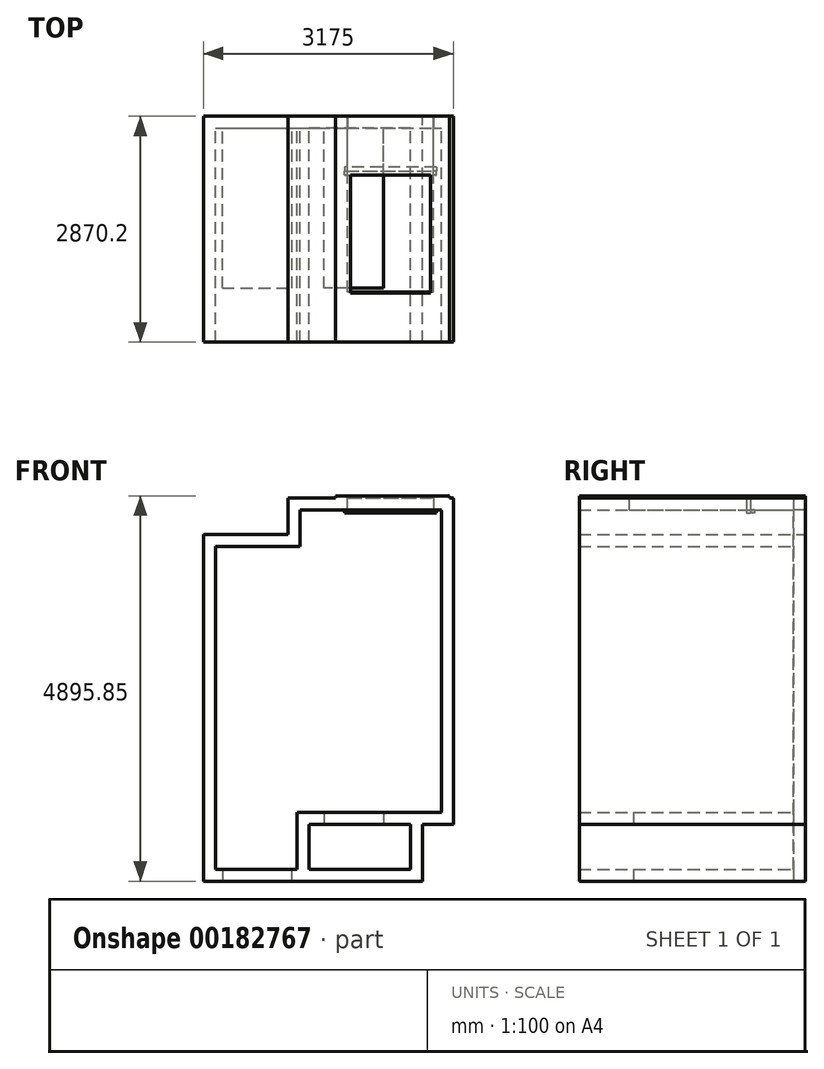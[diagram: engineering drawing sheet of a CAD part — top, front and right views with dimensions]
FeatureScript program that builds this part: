
annotation { "Feature Type Name" : "Feature", "Feature Type Description" : "" }
export const myFeature = defineFeature(function(context is Context, id is Id, definition is map)
    precondition{}
    {
        {
            var Q0;
            Q0=qCreatedBy(makeId("Front.planeOp"),FACE);
            var sketch = newSketch(context, id + "F0", { "sketchPlane" : qUnion([Q0])});
            skLineSegment(sketch, "E0", {"start": v(0, 0) * mm, "end": v(0, 4102.1) * mm});
            skLineSegment(sketch, "E1", {"start": v(0, 0) * mm, "end": v(88.9, 0) * mm});
            skLineSegment(sketch, "E2", {"start": v(88.9, 0) * mm, "end": v(88.9, -152.4) * mm});
            skLineSegment(sketch, "E3", {"start": v(88.9, -152.4) * mm, "end": v(-152.4, -152.4) * mm});
            skLineSegment(sketch, "E4", {"start": v(-152.4, -152.4) * mm, "end": v(-152.4, 4254.5) * mm});
            skLineSegment(sketch, "E5", {"start": v(0, 4102.1) * mm, "end": v(1073.15, 4102.1) * mm});
            skLineSegment(sketch, "E6", {"start": v(-152.4, 4254.5) * mm, "end": v(920.75, 4254.5) * mm});
            skLineSegment(sketch, "E7", {"start": v(1073.15, 4102.1) * mm, "end": v(1073.15, 4565.65) * mm});
            skLineSegment(sketch, "E8", {"start": v(920.75, 4254.5) * mm, "end": v(920.75, 4718.05) * mm});
            skLineSegment(sketch, "E9", {"start": v(1073.15, 4565.65) * mm, "end": v(1676.4, 4565.65) * mm});
            skLineSegment(sketch, "E10", {"start": v(920.75, 4718.05) * mm, "end": v(1524, 4718.05) * mm});
            skLineSegment(sketch, "E11", {"start": v(1524, 4718.05) * mm, "end": v(1524, 4743.45) * mm});
            skLineSegment(sketch, "E12", {"start": v(1524, 4743.45) * mm, "end": v(2971.8, 4743.45) * mm});
            skLineSegment(sketch, "E13", {"start": v(1676.4, 4565.65) * mm, "end": v(1676.4, 4718.05) * mm});
            skLineSegment(sketch, "E14", {"start": v(1676.4, 4718.05) * mm, "end": v(2768.6, 4718.05) * mm});
            skLineSegment(sketch, "E15", {"start": v(2971.8, 4743.45) * mm, "end": v(2971.8, 4718.05) * mm});
            skLineSegment(sketch, "E16", {"start": v(2768.6, 4718.05) * mm, "end": v(2768.6, 4565.65) * mm});
            skLineSegment(sketch, "E17", {"start": v(2768.6, 4565.65) * mm, "end": v(2870.2, 4565.65) * mm});
            skLineSegment(sketch, "E18", {"start": v(2971.8, 4718.05) * mm, "end": v(3022.6, 4718.05) * mm});
            skLineSegment(sketch, "E19", {"start": v(2870.2, 4565.65) * mm, "end": v(2870.2, 723.9) * mm});
            skLineSegment(sketch, "E20", {"start": v(2870.2, 723.9) * mm, "end": v(2133.6, 723.9) * mm});
            skLineSegment(sketch, "E21", {"start": v(2133.6, 723.9) * mm, "end": v(2133.6, 571.5) * mm});
            skLineSegment(sketch, "E22", {"start": v(2133.6, 571.5) * mm, "end": v(2476.5, 571.5) * mm});
            skLineSegment(sketch, "E23", {"start": v(88.9, 0) * mm, "end": v(971.55, 0) * mm});
            skLineSegment(sketch, "E24", {"start": v(88.9, -152.4) * mm, "end": v(971.55, -152.4) * mm});
            skLineSegment(sketch, "E25", {"start": v(971.55, -152.4) * mm, "end": v(971.55, 0) * mm});
            skLineSegment(sketch, "E26", {"start": v(971.55, 0) * mm, "end": v(1035.05, 0) * mm});
            skLineSegment(sketch, "E27", {"start": v(2476.5, 571.5) * mm, "end": v(2476.5, 0) * mm});
            skLineSegment(sketch, "E28", {"start": v(2476.5, 0) * mm, "end": v(1187.45, 0) * mm});
            skLineSegment(sketch, "E29", {"start": v(1035.05, 0) * mm, "end": v(1035.05, 723.9) * mm});
            skLineSegment(sketch, "E30", {"start": v(1035.05, 723.9) * mm, "end": v(1339.85, 723.9) * mm});
            skLineSegment(sketch, "E31", {"start": v(1187.45, 0) * mm, "end": v(1187.45, 571.5) * mm});
            skLineSegment(sketch, "E32", {"start": v(2133.6, 723.9) * mm, "end": v(1377.95, 723.9) * mm});
            skLineSegment(sketch, "E33", {"start": v(2133.6, 571.5) * mm, "end": v(1377.95, 571.5) * mm});
            skLineSegment(sketch, "E34", {"start": v(1377.95, 723.9) * mm, "end": v(1377.95, 571.5) * mm});
            skLineSegment(sketch, "E35", {"start": v(1187.45, 571.5) * mm, "end": v(1339.85, 571.5) * mm});
            skLineSegment(sketch, "E36", {"start": v(1339.85, 723.9) * mm, "end": v(1339.85, 571.5) * mm});
            skLineSegment(sketch, "E37", {"start": v(971.55, -152.4) * mm, "end": v(2628.9, -152.4) * mm});
            skLineSegment(sketch, "E38", {"start": v(2628.9, -152.4) * mm, "end": v(2628.9, 571.5) * mm});
            skLineSegment(sketch, "E39", {"start": v(2628.9, 571.5) * mm, "end": v(3022.6, 571.5) * mm});
            skLineSegment(sketch, "E40", {"start": v(3022.6, 571.5) * mm, "end": v(3022.6, 4718.05) * mm});
            skLineSegment(sketch, "E41", {"start": v(1339.85, 571.5) * mm, "end": v(1377.95, 571.5) * mm});
            skLineSegment(sketch, "E42", {"start": v(1339.85, 723.9) * mm, "end": v(1377.95, 723.9) * mm});
            skLineSegment(sketch, "E43", {"start": v(1676.4, 4565.65) * mm, "end": v(2768.6, 4565.65) * mm});
            skSolve(sketch);
        }
        {
            var Q0;
            Q0=makeQuery(id+"F0.imprint","IMPRINT",FACE,{"disambiguationData":[TD([[makeQuery(id+"F0.imprint","IMPRINT",EDGE,{"derivedFrom":sQuery(id+"F0.wireOp",EDGE,"E0")}),1.0]])]});
            var Q1;
            Q1=makeQuery(id+"F0.imprint","IMPRINT",FACE,{"disambiguationData":[TD([[makeQuery(id+"F0.imprint","IMPRINT",EDGE,{"derivedFrom":sQuery(id+"F0.wireOp",EDGE,"E34")}),-1.0]])]});
            extrude(context, id + "F1", {"entities" : qUnion([Q0, Q1]), "depth" : 2717.8 * mm});
        }
        {
            var Q0;
            Q0=makeQuery(id+"F0.imprint","IMPRINT",FACE,{"disambiguationData":[TD([[makeQuery(id+"F0.imprint","IMPRINT",EDGE,{"derivedFrom":sQuery(id+"F0.wireOp",EDGE,"E2")}),1.0]])]});
            var Q1;
            Q1=makeQuery(id+"F0.imprint","IMPRINT",FACE,{"disambiguationData":[TD([[makeQuery(id+"F0.imprint","IMPRINT",EDGE,{"derivedFrom":sQuery(id+"F0.wireOp",EDGE,"E21")}),-1.0]])]});
            extrude(context, id + "F2", {"entities" : qUnion([Q0, Q1]), "operationType" : NewBodyOperationType.ADD, "depth" : 2717.8 * mm});
        }
        {
            var Q0;
            Q0=makeQuery(id+"F0.imprint","IMPRINT",FACE,{"disambiguationData":[TD([[makeQuery(id+"F0.imprint","IMPRINT",EDGE,{"derivedFrom":sQuery(id+"F0.wireOp",EDGE,"E21")}),-1.0]])]});
            var Q1;
            Q1=makeQuery(id+"F0.imprint","IMPRINT",FACE,{"disambiguationData":[TD([[makeQuery(id+"F0.imprint","IMPRINT",EDGE,{"derivedFrom":sQuery(id+"F0.wireOp",EDGE,"E2")}),1.0]])]});
            extrude(context, id + "F3", {"entities" : qUnion([Q0, Q1]), "operationType" : NewBodyOperationType.REMOVE, "depth" : 2032 * mm});
        }
        {
            var Q0;
            Q0=makeQuery(id+"F0.imprint","IMPRINT",FACE,{"disambiguationData":[TD([[makeQuery(id+"F0.imprint","IMPRINT",EDGE,{"derivedFrom":sQuery(id+"F0.wireOp",EDGE,"E0")}),-1.0]])]});
            var Q1;
            Q1=makeQuery(id+"F0.imprint","IMPRINT",FACE,{"disambiguationData":[TD([[makeQuery(id+"F0.imprint","IMPRINT",EDGE,{"derivedFrom":sQuery(id+"F0.wireOp",EDGE,"E0")}),1.0]])]});
            var Q2;
            Q2=makeQuery(id+"F0.imprint","IMPRINT",FACE,{"disambiguationData":[TD([[makeQuery(id+"F0.imprint","IMPRINT",EDGE,{"derivedFrom":sQuery(id+"F0.wireOp",EDGE,"E22")}),-1.0]])]});
            var Q3;
            Q3=makeQuery(id+"F0.imprint","IMPRINT",FACE,{"disambiguationData":[TD([[makeQuery(id+"F0.imprint","IMPRINT",EDGE,{"derivedFrom":sQuery(id+"F0.wireOp",EDGE,"E21")}),-1.0]])]});
            var Q4;
            Q4=makeQuery(id+"F0.imprint","IMPRINT",FACE,{"disambiguationData":[TD([[makeQuery(id+"F0.imprint","IMPRINT",EDGE,{"derivedFrom":sQuery(id+"F0.wireOp",EDGE,"E34")}),-1.0]])]});
            var Q5;
            Q5=makeQuery(id+"F0.imprint","IMPRINT",FACE,{"disambiguationData":[TD([[makeQuery(id+"F0.imprint","IMPRINT",EDGE,{"derivedFrom":sQuery(id+"F0.wireOp",EDGE,"E2")}),1.0]])]});
            extrude(context, id + "F4", {"entities" : qUnion([Q0, Q1, Q2, Q3, Q4, Q5]), "operationType" : NewBodyOperationType.ADD, "oppositeDirection" : true, "depth" : 152.4 * mm});
        }
        {
            var Q0;
            Q0=makeQuery(id+"F0.imprint","IMPRINT",FACE,{"disambiguationData":[TD([[makeQuery(id+"F0.imprint","IMPRINT",EDGE,{"derivedFrom":sQuery(id+"F0.wireOp",EDGE,"E13")}),-1.0]])]});
            extrude(context, id + "F5", {"entities" : qUnion([Q0]), "depth" : 546.1 * mm});
        }
        {
            var Q0;
            Q0=makeQuery(id+"F5.opExtrude","CAP_FACE",FACE,{"disambiguationData":[OSD([sQuery(id+"F0.wireOp",EDGE,"E13"),sQuery(id+"F0.wireOp",EDGE,"E14"),sQuery(id+"F0.wireOp",EDGE,"E16"),sQuery(id+"F0.wireOp",EDGE,"E43")])],"isStart":true});
            extrude(context, id + "F6", {"entities" : qUnion([Q0]), "depth" : 152.4 * mm});
        }
        {
            var Q0;
            {var subQ0=sQuery(id+"F0.wireOp",EDGE,"E14");Q0=makeQuery(id+"F4.boolean.opBoolean","MERGE",FACE,{"derivedFrom":[makeQuery(id+"F1.opExtrude","SWEPT_FACE",FACE,{"disambiguationData":[OSD([subQ0])]}),makeQuery(id+"F4.opExtrude","SWEPT_FACE",FACE,{"disambiguationData":[OSD([subQ0])]})]});}
            var sketch = newSketch(context, id + "F7", { "sketchPlane" : qUnion([Q0])});
            skLineSegment(sketch, "E44", {"start": v(1676.4, 2717.8) * mm, "end": v(1676.4, -152.4) * mm, "construction": true});
            skLineSegment(sketch, "E45", {"start": v(2768.6, 2717.8) * mm, "end": v(2768.6, -152.4) * mm, "construction": true});
            skLineSegment(sketch, "E46", {"start": v(1676.4, 2717.8) * mm, "end": v(2768.6, 2717.8) * mm, "construction": true});
            skLineSegment(sketch, "E47", {"start": v(2768.6, 2095.5) * mm, "end": v(1676.4, 2095.5) * mm});
            skLineSegment(sketch, "E48", {"start": v(1676.4, 2095.5) * mm, "end": v(1676.4, 596.9) * mm});
            skLineSegment(sketch, "E49", {"start": v(1676.4, 596.9) * mm, "end": v(2768.6, 596.9) * mm});
            skLineSegment(sketch, "E50", {"start": v(2768.6, 596.9) * mm, "end": v(2768.6, 2095.5) * mm});
            skLineSegment(sketch, "E51", {"start": v(2730.5, 2095.5) * mm, "end": v(2730.5, 596.9) * mm});
            skLineSegment(sketch, "E52", {"start": v(1714.5, 596.9) * mm, "end": v(1714.5, 2095.5) * mm});
            skSolve(sketch);
        }
        {
            var Q0;
            {var subQ0=sQuery(id+"F7.wireOp",EDGE,"E51");Q0=makeQuery(id+"F7.imprint","IMPRINT",FACE,{"disambiguationData":[TD([[makeQuery(id+"F7.imprint","IMPRINT",EDGE,{"derivedFrom":subQ0}),-1.0]])]});}
            extrude(context, id + "F8", {"entities" : qUnion([Q0]), "operationType" : NewBodyOperationType.REMOVE, "endBound" : BoundingType.UP_TO_NEXT, "oppositeDirection" : true, "depth" : 25.4 * mm});
        }
        {
            var Q0;
            Q0=makeQuery(id+"F5.opExtrude","CAP_FACE",FACE,{"disambiguationData":[OSD([sQuery(id+"F0.wireOp",EDGE,"E13"),sQuery(id+"F0.wireOp",EDGE,"E14"),sQuery(id+"F0.wireOp",EDGE,"E16"),sQuery(id+"F0.wireOp",EDGE,"E43")])],"isStart":false});
            var sketch = newSketch(context, id + "F9", { "sketchPlane" : qUnion([Q0])});
            skLineSegment(sketch, "E53", {"start": v(1676.4, 4565.65) * mm, "end": v(2768.6, 4565.65) * mm, "construction": true});
            skLineSegment(sketch, "E54", {"start": v(2768.6, 4718.05) * mm, "end": v(2768.6, 4565.65) * mm, "construction": true});
            skLineSegment(sketch, "E55", {"start": v(1676.4, 4718.05) * mm, "end": v(1676.4, 4565.65) * mm, "construction": true});
            skLineSegment(sketch, "E56", {"start": v(1676.4, 4718.05) * mm, "end": v(2768.6, 4718.05) * mm, "construction": true});
            skLineSegment(sketch, "E57", {"start": v(2768.6, 4718.05) * mm, "end": v(2768.6, 4565.65) * mm});
            skLineSegment(sketch, "E58", {"start": v(2806.7, 4565.65) * mm, "end": v(2768.6, 4565.65) * mm});
            skLineSegment(sketch, "E59", {"start": v(2768.6, 4565.65) * mm, "end": v(2768.6, 4718.05) * mm});
            skLineSegment(sketch, "E60", {"start": v(2768.6, 4718.05) * mm, "end": v(1676.4, 4718.05) * mm});
            skLineSegment(sketch, "E61", {"start": v(1676.4, 4718.05) * mm, "end": v(1676.4, 4565.65) * mm});
            skLineSegment(sketch, "E62", {"start": v(1676.4, 4565.65) * mm, "end": v(1638.3, 4565.65) * mm});
            skLineSegment(sketch, "E63", {"start": v(2806.7, 4565.65) * mm, "end": v(2806.7, 4527.55) * mm});
            skLineSegment(sketch, "E64", {"start": v(1638.3, 4565.65) * mm, "end": v(1638.3, 4527.55) * mm});
            skLineSegment(sketch, "E65", {"start": v(1638.3, 4527.55) * mm, "end": v(2806.7, 4527.55) * mm});
            skLineSegment(sketch, "E66", {"start": v(1676.4, 4565.65) * mm, "end": v(2768.6, 4565.65) * mm});
            skSolve(sketch);
        }
        {
            var Q0;
            Q0=makeQuery(id+"F9.imprint","IMPRINT",FACE,{"disambiguationData":[TD([[makeQuery(id+"F9.imprint","IMPRINT",EDGE,{"derivedFrom":sQuery(id+"F9.wireOp",EDGE,"E57")}),-1.0]])]});
            var Q1;
            Q1=makeQuery(id+"F9.imprint","IMPRINT",FACE,{"disambiguationData":[TD([[makeQuery(id+"F9.imprint","IMPRINT",EDGE,{"derivedFrom":sQuery(id+"F9.wireOp",EDGE,"E58")}),1.0]])]});
            extrude(context, id + "F10", {"entities" : qUnion([Q0, Q1]), "depth" : 50.8 * mm});
        }
        {
            var Q0;
            Q0=makeQuery(id+"F9.imprint","IMPRINT",FACE,{"disambiguationData":[TD([[makeQuery(id+"F9.imprint","IMPRINT",EDGE,{"derivedFrom":sQuery(id+"F9.wireOp",EDGE,"E58")}),1.0]])]});
            extrude(context, id + "F11", {"entities" : qUnion([Q0]), "oppositeDirection" : true, "depth" : 50.8 * mm});
        }
        {
            var Q0;
            {var subQ0=sQuery(id+"F0.wireOp",EDGE,"E13");Q0=makeQuery(id+"F4.boolean.opBoolean","MERGE",FACE,{"derivedFrom":[makeQuery(id+"F1.opExtrude","SWEPT_FACE",FACE,{"disambiguationData":[OSD([subQ0])]}),makeQuery(id+"F4.opExtrude","SWEPT_FACE",FACE,{"disambiguationData":[OSD([subQ0])]})]});}
            var sketch = newSketch(context, id + "F12", { "sketchPlane" : qUnion([Q0])});
            skLineSegment(sketch, "E67", {"start": v(-2717.8, 4565.65) * mm, "end": v(-2717.8, 4718.05) * mm, "construction": true});
            skLineSegment(sketch, "E68", {"start": v(-2717.8, 4565.65) * mm, "end": v(-2082.8, 4565.65) * mm, "construction": true});
            skLineSegment(sketch, "E69.bottom", {"start": v(-2082.8, 4565.65) * mm, "end": v(-2717.8, 4565.65) * mm});
            skLineSegment(sketch, "E69.top", {"start": v(-2082.8, 4718.05) * mm, "end": v(-2717.8, 4718.05) * mm});
            skLineSegment(sketch, "E69.left", {"start": v(-2082.8, 4565.65) * mm, "end": v(-2082.8, 4718.05) * mm});
            skLineSegment(sketch, "E69.right", {"start": v(-2717.8, 4565.65) * mm, "end": v(-2717.8, 4718.05) * mm});
            skSolve(sketch);
        }
        {
            var Q0;
            Q0=makeQuery(id+"F12.imprint","IMPRINT",FACE,{"disambiguationData":[TD([[makeQuery(id+"F12.imprint","IMPRINT",EDGE,{"derivedFrom":sQuery(id+"F12.wireOp",EDGE,"E69.bottom")}),1.0]])]});
            extrude(context, id + "F13", {"entities" : qUnion([Q0]), "operationType" : NewBodyOperationType.ADD, "depth" : 1092.2 * mm});
        }
    });
